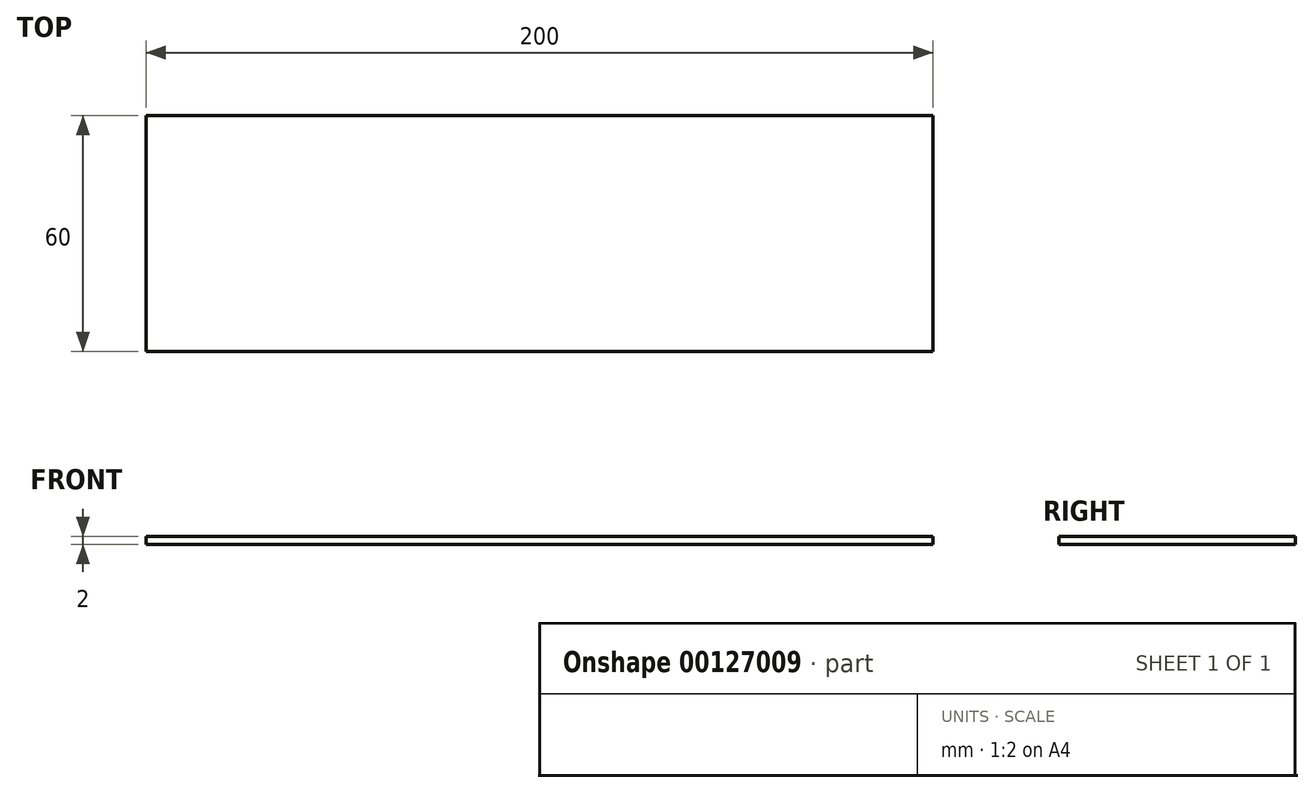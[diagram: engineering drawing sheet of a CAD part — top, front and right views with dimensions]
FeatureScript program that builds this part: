
annotation { "Feature Type Name" : "Feature", "Feature Type Description" : "" }
export const myFeature = defineFeature(function(context is Context, id is Id, definition is map)
    precondition{}
    {
        {
            var Q0;
            Q0=qCreatedBy(makeId("Top.planeOp"),FACE);
            var sketch = newSketch(context, id + "F0", { "sketchPlane" : qUnion([Q0])});
            skLineSegment(sketch, "E0.bottom", {"start": v(100, -30) * mm, "end": v(-100, -30) * mm});
            skLineSegment(sketch, "E0.top", {"start": v(100, 30) * mm, "end": v(-100, 30) * mm});
            skLineSegment(sketch, "E0.left", {"start": v(100, -30) * mm, "end": v(100, 30) * mm});
            skLineSegment(sketch, "E0.right", {"start": v(-100, -30) * mm, "end": v(-100, 30) * mm});
            skPoint(sketch, "E0.middle", {"position": v(0, 0) * mm});
            skSolve(sketch);
        }
        {
            var Q0;
            Q0 = qSketchRegion(id + "F0", true);
            extrude(context, id + "F1", {"entities" : qUnion([Q0]), "depth" : 2 * mm});
        }
    });
